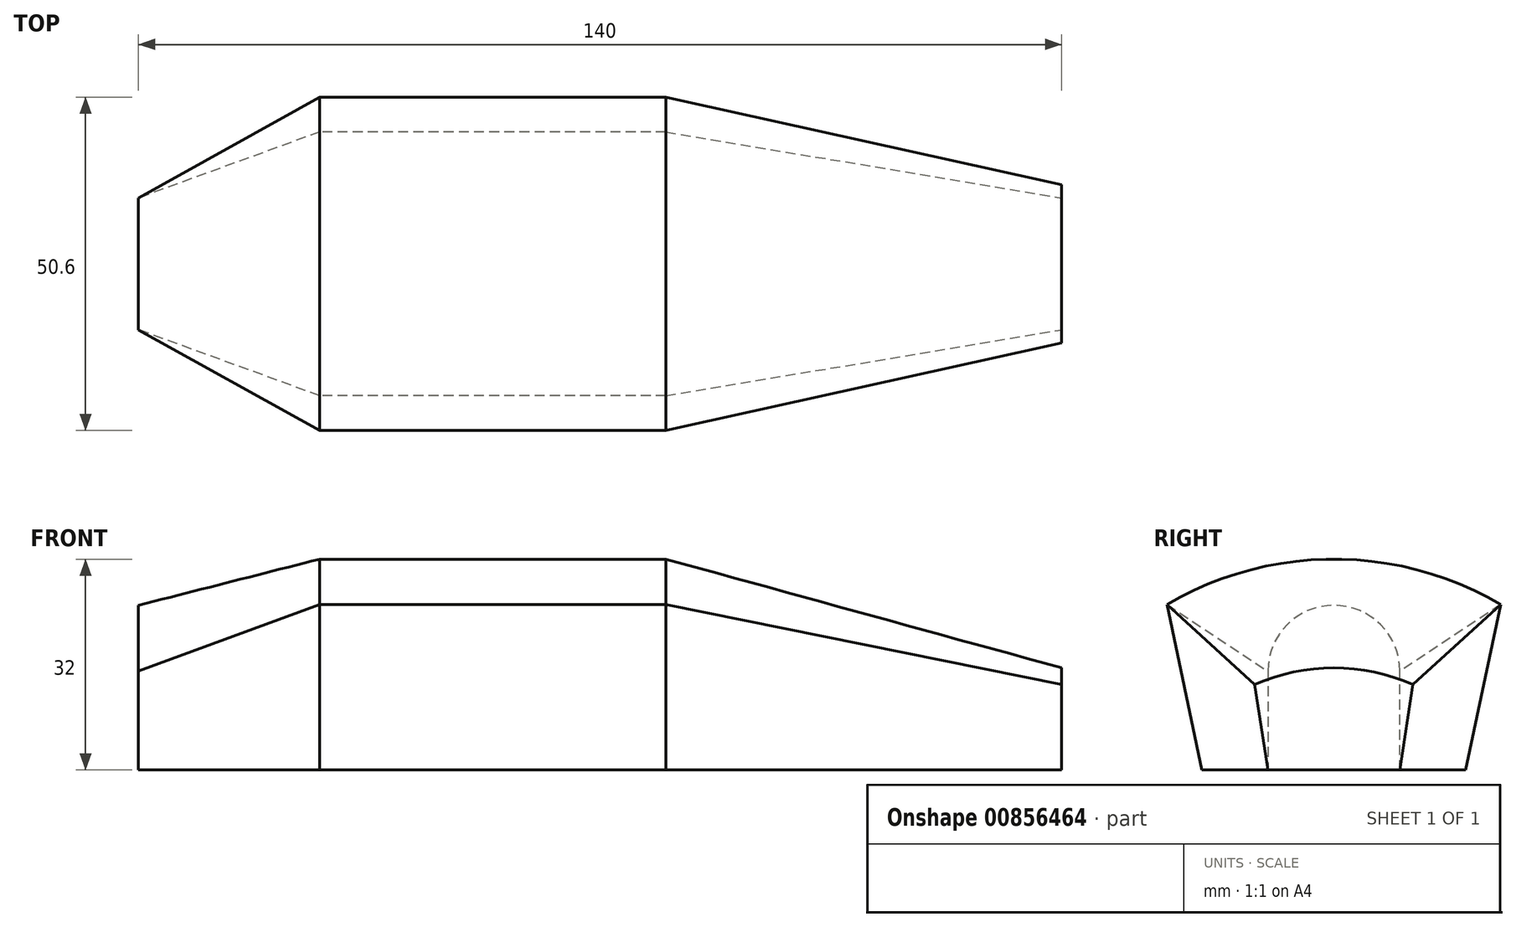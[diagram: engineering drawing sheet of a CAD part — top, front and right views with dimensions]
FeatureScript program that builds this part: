
annotation { "Feature Type Name" : "Feature", "Feature Type Description" : "" }
export const myFeature = defineFeature(function(context is Context, id is Id, definition is map)
    precondition{}
    {
        {
            var Q0;
            Q0=qCreatedBy(makeId("Right.planeOp"),FACE);
            var sketch = newSketch(context, id + "F0", { "sketchPlane" : qUnion([Q0])});
            skLineSegment(sketch, "E0", {"start": v(-25.3, 25.13) * mm, "end": v(-20, 0) * mm});
            skLineSegment(sketch, "E1", {"start": v(-20, 0) * mm, "end": v(20, 0) * mm});
            skLineSegment(sketch, "E2", {"start": v(20, 0) * mm, "end": v(25.3, 25.13) * mm});
            skArc(sketch, "E3", {"start": v(25.3, 25.13) * mm, "mid": v(0, 32) * mm, "end": v(-25.3, 25.13) * mm});
            skSolve(sketch);
        }
        {
            var Q0;
            Q0=makeQuery(id+"F0.imprint","IMPRINT",FACE,{"disambiguationData":[TD([[makeQuery(id+"F0.imprint","IMPRINT",EDGE,{"derivedFrom":sQuery(id+"F0.wireOp",EDGE,"E0")}),1.0]])]});
            extrude(context, id + "F1", {"entities" : qUnion([Q0]), "depth" : 10 * mm, "offsetDistance" : 25 * mm, "hasSecondDirection" : true, "secondDirectionOppositeDirection" : true, "secondDirectionDepth" : 42.5 * mm});
        }
        {
            var Q0;
            Q0=qCreatedBy(makeId("Right.planeOp"),FACE);
            cPlane(context, id + "F2", {"entities" : qUnion([Q0]), "cplaneType" : CPlaneType.OFFSET, "offset" : 70 * mm, "width" : 150 * mm, "height" : 150 * mm});
        }
        {
            var Q0;
            Q0=qCreatedBy(id+"F2.planeOp",FACE);
            var sketch = newSketch(context, id + "F3", { "sketchPlane" : qUnion([Q0])});
            skLineSegment(sketch, "E4", {"start": v(-12, 13) * mm, "end": v(-10, 0) * mm});
            skLineSegment(sketch, "E5", {"start": v(-10, 0) * mm, "end": v(10, 0) * mm});
            skLineSegment(sketch, "E6", {"start": v(10, 0) * mm, "end": v(12, 13) * mm});
            skArc(sketch, "E7", {"start": v(12, 13) * mm, "mid": v(0, 15.5) * mm, "end": v(-12, 13) * mm});
            skSolve(sketch);
        }
        {
            var Q1;
            Q1=makeQuery(id+"F1.opExtrude","CAP_FACE",FACE,{"disambiguationData":[OSD([sQuery(id+"F0.wireOp",EDGE,"E0"),sQuery(id+"F0.wireOp",EDGE,"E1"),sQuery(id+"F0.wireOp",EDGE,"E2"),sQuery(id+"F0.wireOp",EDGE,"E3")])],"isStart":false});
            var Q2;
            Q2=makeQuery(id+"F3.imprint","IMPRINT",FACE,{"disambiguationData":[TD([[makeQuery(id+"F3.imprint","IMPRINT",EDGE,{"derivedFrom":sQuery(id+"F3.wireOp",EDGE,"E4")}),1.0]])]});
            loft(context, id + "F4", {"operationType" : NewBodyOperationType.ADD, "sheetProfilesArray" : [{ "sheetProfileEntities" : qUnion([Q1]) }, { "sheetProfileEntities" : qUnion([Q2]) }]});
        }
        {
            var Q0;
            Q0=qCreatedBy(makeId("Right.planeOp"),FACE);
            cPlane(context, id + "F5", {"entities" : qUnion([Q0]), "cplaneType" : CPlaneType.OFFSET, "offset" : 70 * mm, "oppositeDirection" : true, "width" : 150 * mm, "height" : 150 * mm});
        }
        {
            var Q0;
            Q0=qCreatedBy(id+"F5.planeOp",FACE);
            var sketch = newSketch(context, id + "F6", { "sketchPlane" : qUnion([Q0])});
            skLineSegment(sketch, "E8", {"start": v(-10, 15) * mm, "end": v(-10, 0) * mm});
            skLineSegment(sketch, "E9", {"start": v(-10, 0) * mm, "end": v(10, 0) * mm});
            skLineSegment(sketch, "E10", {"start": v(10, 0) * mm, "end": v(10, 15) * mm});
            skArc(sketch, "E11", {"start": v(10, 15) * mm, "mid": v(0, 25) * mm, "end": v(-10, 15) * mm});
            skSolve(sketch);
        }
        {
            var Q1;
            Q1=makeQuery(id+"F1.opExtrude","CAP_FACE",FACE,{"disambiguationData":[OSD([sQuery(id+"F0.wireOp",EDGE,"E0"),sQuery(id+"F0.wireOp",EDGE,"E1"),sQuery(id+"F0.wireOp",EDGE,"E2"),sQuery(id+"F0.wireOp",EDGE,"E3")])],"isStart":true});
            var Q2;
            Q2=makeQuery(id+"F6.imprint","IMPRINT",FACE,{"disambiguationData":[TD([[makeQuery(id+"F6.imprint","IMPRINT",EDGE,{"derivedFrom":sQuery(id+"F6.wireOp",EDGE,"E8")}),1.0]])]});
            loft(context, id + "F7", {"operationType" : NewBodyOperationType.ADD, "sheetProfilesArray" : [{ "sheetProfileEntities" : qUnion([Q1]) }, { "sheetProfileEntities" : qUnion([Q2]) }]});
        }
    });
